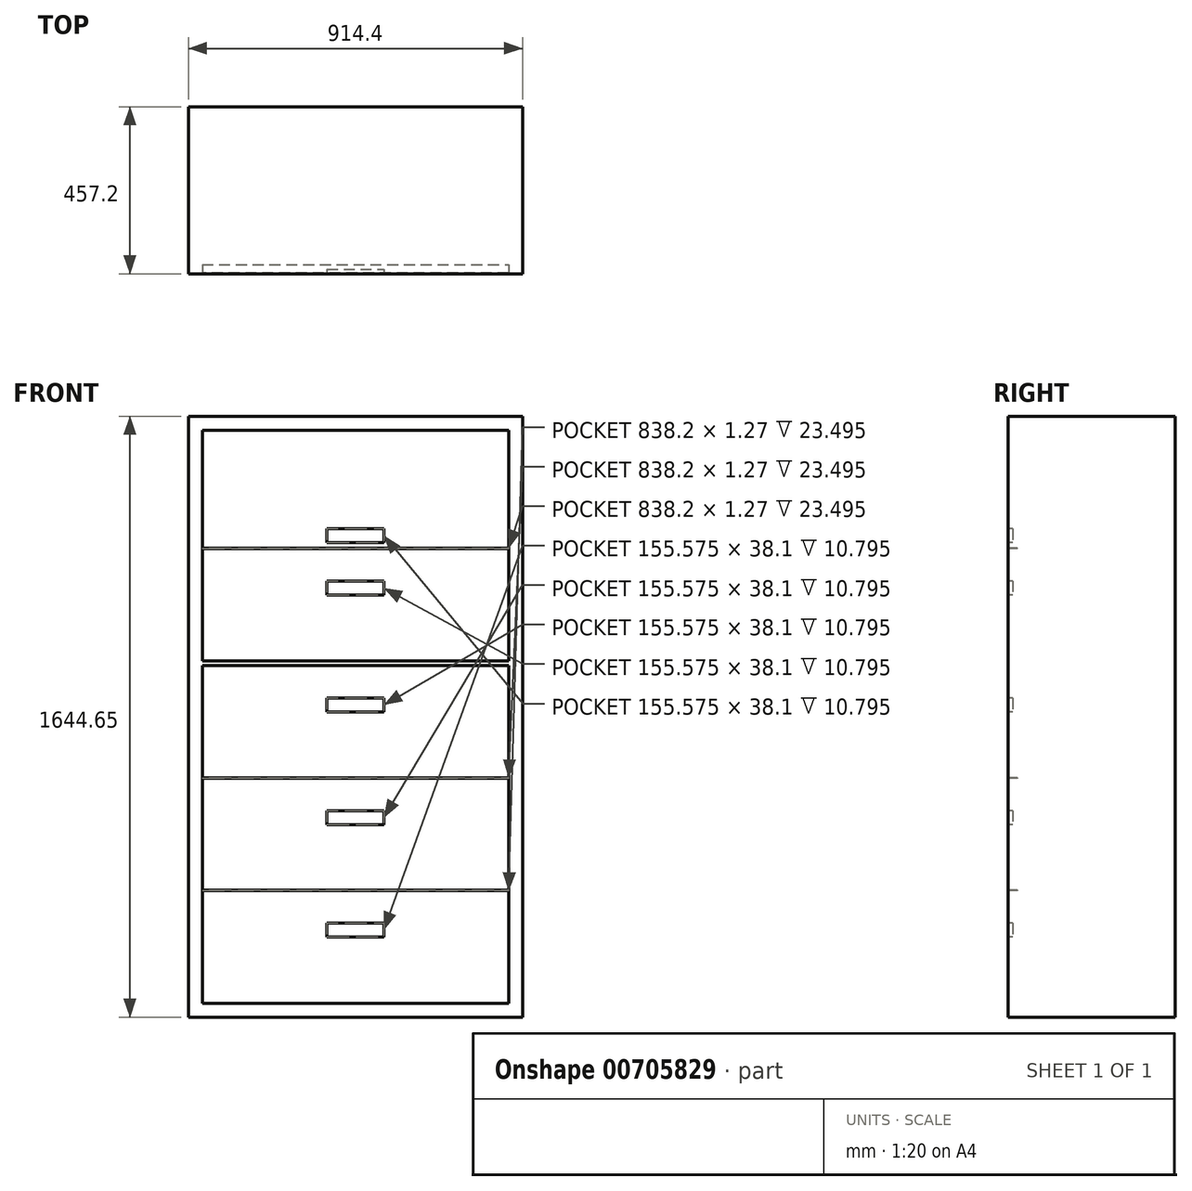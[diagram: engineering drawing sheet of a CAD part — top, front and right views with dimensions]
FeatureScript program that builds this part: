
annotation { "Feature Type Name" : "Feature", "Feature Type Description" : "" }
export const myFeature = defineFeature(function(context is Context, id is Id, definition is map)
    precondition{}
    {
        {
            var Q0;
            Q0=qCreatedBy(makeId("Top.planeOp"),FACE);
            var sketch = newSketch(context, id + "F0", { "sketchPlane" : qUnion([Q0])});
            skLineSegment(sketch, "E0.bottom", {"start": v(0, 0) * mm, "end": v(914.4, 0) * mm});
            skLineSegment(sketch, "E0.top", {"start": v(0, 457.2) * mm, "end": v(914.4, 457.2) * mm});
            skLineSegment(sketch, "E0.left", {"start": v(0, 0) * mm, "end": v(0, 457.2) * mm});
            skLineSegment(sketch, "E0.right", {"start": v(914.4, 0) * mm, "end": v(914.4, 457.2) * mm});
            skSolve(sketch);
        }
        {
            var Q0;
            Q0 = qSketchRegion(id + "F0", true);
            extrude(context, id + "F1", {"entities" : qUnion([Q0]), "depth" : 1644.65 * mm, "offsetDistance" : 25.4 * mm});
        }
        {
            var Q0;
            Q0=makeQuery(id+"F1.opExtrude","SWEPT_FACE",FACE,{"disambiguationData":[OSD([sQuery(id+"F0.wireOp",EDGE,"E0.bottom")])]});
            var sketch = newSketch(context, id + "F2", { "sketchPlane" : qUnion([Q0])});
            skLineSegment(sketch, "E1.0.0", {"start": v(0, 0) * mm, "end": v(914.4, 0) * mm});
            skLineSegment(sketch, "E1.0.1", {"start": v(914.4, 0) * mm, "end": v(914.4, 1644.65) * mm});
            skLineSegment(sketch, "E1.0.2", {"start": v(914.4, 1644.65) * mm, "end": v(0, 1644.65) * mm});
            skLineSegment(sketch, "E1.0.3", {"start": v(0, 1644.65) * mm, "end": v(0, 0) * mm});
            skLineSegment(sketch, "E2.0", {"start": v(38.1, 1606.55) * mm, "end": v(38.1, 38.1) * mm});
            skLineSegment(sketch, "E2.1", {"start": v(876.3, 1606.55) * mm, "end": v(38.1, 1606.55) * mm});
            skLineSegment(sketch, "E2.2", {"start": v(876.3, 38.1) * mm, "end": v(876.3, 1606.55) * mm});
            skLineSegment(sketch, "E2.3", {"start": v(38.1, 38.1) * mm, "end": v(876.3, 38.1) * mm});
            skLineSegment(sketch, "E3", {"start": v(38.1, 346.08) * mm, "end": v(876.3, 346.08) * mm});
            skLineSegment(sketch, "E4", {"start": v(38.1, 654.05) * mm, "end": v(876.3, 654.05) * mm});
            skLineSegment(sketch, "E5", {"start": v(38.1, 962.03) * mm, "end": v(876.3, 962.03) * mm});
            skLineSegment(sketch, "E6", {"start": v(38.1, 974.73) * mm, "end": v(876.3, 974.73) * mm});
            skLineSegment(sketch, "E7", {"start": v(38.1, 1282.7) * mm, "end": v(876.3, 1282.7) * mm});
            skLineSegment(sketch, "E8", {"start": v(457.2, 1606.55) * mm, "end": v(457.2, 38.1) * mm, "construction": true});
            skLineSegment(sketch, "E9.bottom", {"start": v(379.41, 257.18) * mm, "end": v(534.99, 257.18) * mm});
            skLineSegment(sketch, "E9.top", {"start": v(379.41, 219.08) * mm, "end": v(534.99, 219.08) * mm});
            skLineSegment(sketch, "E9.left", {"start": v(379.41, 257.18) * mm, "end": v(379.41, 219.08) * mm});
            skLineSegment(sketch, "E9.right", {"start": v(534.99, 257.18) * mm, "end": v(534.99, 219.08) * mm});
            skPoint(sketch, "E10", {"position": v(457.2, 257.18) * mm});
            skLineSegment(sketch, "E11.bottom", {"start": v(379.41, 565.15) * mm, "end": v(534.99, 565.15) * mm});
            skLineSegment(sketch, "E11.top", {"start": v(379.41, 527.05) * mm, "end": v(534.99, 527.05) * mm});
            skLineSegment(sketch, "E11.left", {"start": v(379.41, 565.15) * mm, "end": v(379.41, 527.05) * mm});
            skLineSegment(sketch, "E11.right", {"start": v(534.99, 565.15) * mm, "end": v(534.99, 527.05) * mm});
            skLineSegment(sketch, "E12.bottom", {"start": v(379.41, 873.13) * mm, "end": v(534.99, 873.13) * mm});
            skLineSegment(sketch, "E12.top", {"start": v(379.41, 835.03) * mm, "end": v(534.99, 835.03) * mm});
            skLineSegment(sketch, "E12.left", {"start": v(379.41, 873.13) * mm, "end": v(379.41, 835.03) * mm});
            skLineSegment(sketch, "E12.right", {"start": v(534.99, 873.13) * mm, "end": v(534.99, 835.03) * mm});
            skLineSegment(sketch, "E13.bottom", {"start": v(379.41, 1193.8) * mm, "end": v(534.99, 1193.8) * mm});
            skLineSegment(sketch, "E13.top", {"start": v(379.41, 1155.7) * mm, "end": v(534.99, 1155.7) * mm});
            skLineSegment(sketch, "E13.left", {"start": v(379.41, 1193.8) * mm, "end": v(379.41, 1155.7) * mm});
            skLineSegment(sketch, "E13.right", {"start": v(534.99, 1193.8) * mm, "end": v(534.99, 1155.7) * mm});
            skLineSegment(sketch, "E14.bottom", {"start": v(379.41, 1336.68) * mm, "end": v(534.99, 1336.68) * mm});
            skLineSegment(sketch, "E14.top", {"start": v(379.41, 1298.58) * mm, "end": v(534.99, 1298.58) * mm});
            skLineSegment(sketch, "E14.left", {"start": v(379.41, 1336.68) * mm, "end": v(379.41, 1298.58) * mm});
            skLineSegment(sketch, "E14.right", {"start": v(534.99, 1336.68) * mm, "end": v(534.99, 1298.58) * mm});
            skPoint(sketch, "E15", {"position": v(457.2, 1336.68) * mm});
            skPoint(sketch, "E16", {"position": v(457.2, 1193.8) * mm});
            skPoint(sketch, "E17", {"position": v(457.2, 873.13) * mm});
            skPoint(sketch, "E18", {"position": v(457.2, 565.15) * mm});
            skLineSegment(sketch, "E19", {"start": v(38.1, 347.35) * mm, "end": v(876.3, 347.35) * mm});
            skLineSegment(sketch, "E20", {"start": v(38.1, 655.32) * mm, "end": v(876.3, 655.32) * mm});
            skLineSegment(sketch, "E21", {"start": v(38.1, 1283.97) * mm, "end": v(876.3, 1283.97) * mm});
            skSolve(sketch);
        }
        {
            var Q0;
            {var subQ0=sQuery(id+"F2.wireOp",EDGE,"E2.3");Q0=makeQuery(id+"F2.imprint","IMPRINT",FACE,{"disambiguationData":[TD([[makeQuery(id+"F2.imprint","IMPRINT",EDGE,{"derivedFrom":subQ0}),1.0]])]});}
            var Q1;
            {var subQ0=sQuery(id+"F2.wireOp",EDGE,"E4");Q1=makeQuery(id+"F2.imprint","IMPRINT",FACE,{"disambiguationData":[TD([[makeQuery(id+"F2.imprint","IMPRINT",EDGE,{"derivedFrom":subQ0}),-1.0]])]});}
            var Q2;
            {var subQ0=sQuery(id+"F2.wireOp",EDGE,"E5");Q2=makeQuery(id+"F2.imprint","IMPRINT",FACE,{"disambiguationData":[TD([[makeQuery(id+"F2.imprint","IMPRINT",EDGE,{"derivedFrom":subQ0}),-1.0]])]});}
            var Q3;
            {var subQ1=sQuery(id+"F2.wireOp",EDGE,"E6");Q3=makeQuery(id+"F2.imprint","IMPRINT",FACE,{"disambiguationData":[TD([[makeQuery(id+"F2.imprint","IMPRINT",EDGE,{"derivedFrom":subQ1}),1.0]])]});}
            var Q4;
            {var subQ1=sQuery(id+"F2.wireOp",EDGE,"E2.1");Q4=makeQuery(id+"F2.imprint","IMPRINT",FACE,{"disambiguationData":[TD([[makeQuery(id+"F2.imprint","IMPRINT",EDGE,{"derivedFrom":subQ1}),1.0]])]});}
            extrude(context, id + "F3", {"entities" : qUnion([Q0, Q1, Q2, Q3, Q4]), "operationType" : NewBodyOperationType.REMOVE, "oppositeDirection" : true, "depth" : 1.9 * mm, "offsetDistance" : 25.4 * mm});
        }
        {
            var Q0;
            {var subQ0=sQuery(id+"F2.wireOp",EDGE,"E3");Q0=makeQuery(id+"F2.imprint","IMPRINT",FACE,{"disambiguationData":[TD([[makeQuery(id+"F2.imprint","IMPRINT",EDGE,{"derivedFrom":subQ0}),1.0]])]});}
            var Q1;
            {var subQ0=sQuery(id+"F2.wireOp",EDGE,"E4");Q1=makeQuery(id+"F2.imprint","IMPRINT",FACE,{"disambiguationData":[TD([[makeQuery(id+"F2.imprint","IMPRINT",EDGE,{"derivedFrom":subQ0}),1.0]])]});}
            var Q2;
            {var subQ0=sQuery(id+"F2.wireOp",EDGE,"E7");Q2=makeQuery(id+"F2.imprint","IMPRINT",FACE,{"disambiguationData":[TD([[makeQuery(id+"F2.imprint","IMPRINT",EDGE,{"derivedFrom":subQ0}),1.0]])]});}
            extrude(context, id + "F4", {"entities" : qUnion([Q0, Q1, Q2]), "operationType" : NewBodyOperationType.REMOVE, "oppositeDirection" : true, "depth" : 25.4 * mm, "offsetDistance" : 25.4 * mm});
        }
        {
            var Q0;
            Q0=makeQuery(id+"F2.imprint","IMPRINT",FACE,{"disambiguationData":[TD([[makeQuery(id+"F2.imprint","IMPRINT",EDGE,{"derivedFrom":sQuery(id+"F2.wireOp",EDGE,"E14.bottom")}),-1.0]])]});
            var Q1;
            Q1=makeQuery(id+"F2.imprint","IMPRINT",FACE,{"disambiguationData":[TD([[makeQuery(id+"F2.imprint","IMPRINT",EDGE,{"derivedFrom":sQuery(id+"F2.wireOp",EDGE,"E13.bottom")}),-1.0]])]});
            var Q2;
            Q2=makeQuery(id+"F2.imprint","IMPRINT",FACE,{"disambiguationData":[TD([[makeQuery(id+"F2.imprint","IMPRINT",EDGE,{"derivedFrom":sQuery(id+"F2.wireOp",EDGE,"E12.bottom")}),-1.0]])]});
            var Q3;
            Q3=makeQuery(id+"F2.imprint","IMPRINT",FACE,{"disambiguationData":[TD([[makeQuery(id+"F2.imprint","IMPRINT",EDGE,{"derivedFrom":sQuery(id+"F2.wireOp",EDGE,"E11.bottom")}),-1.0]])]});
            var Q4;
            Q4=makeQuery(id+"F2.imprint","IMPRINT",FACE,{"disambiguationData":[TD([[makeQuery(id+"F2.imprint","IMPRINT",EDGE,{"derivedFrom":sQuery(id+"F2.wireOp",EDGE,"E9.bottom")}),-1.0]])]});
            extrude(context, id + "F5", {"entities" : qUnion([Q0, Q1, Q2, Q3, Q4]), "operationType" : NewBodyOperationType.REMOVE, "oppositeDirection" : true, "depth" : 12.7 * mm, "offsetDistance" : 25.4 * mm});
        }
    });
